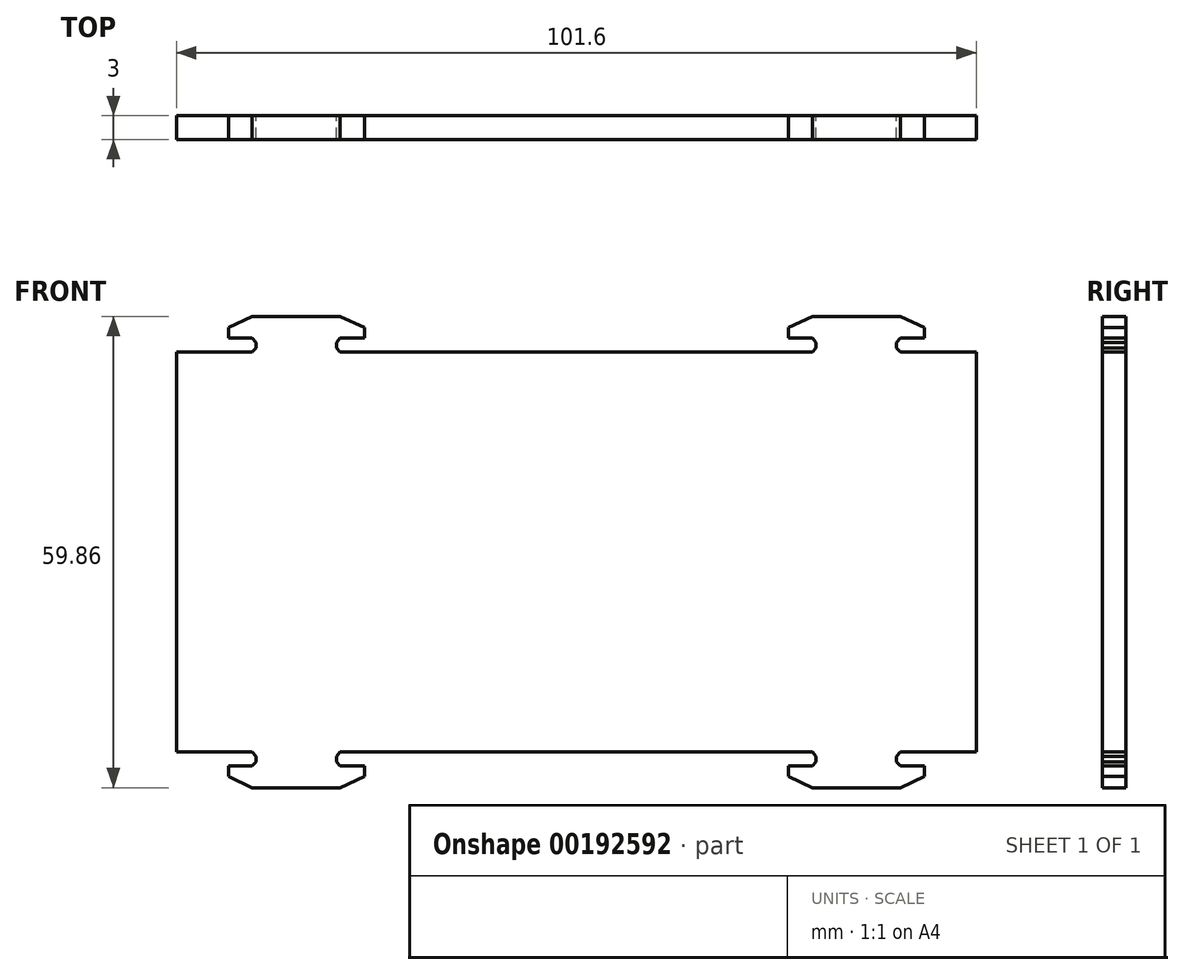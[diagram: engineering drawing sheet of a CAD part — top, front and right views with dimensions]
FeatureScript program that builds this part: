
annotation { "Feature Type Name" : "Feature", "Feature Type Description" : "" }
export const myFeature = defineFeature(function(context is Context, id is Id, definition is map)
    precondition{}
    {
        {
            var Q0;
            Q0=qCreatedBy(makeId("Front.planeOp"),FACE);
            var sketch = newSketch(context, id + "F0", { "sketchPlane" : qUnion([Q0])});
            skLineSegment(sketch, "E0.bottom", {"start": v(50.8, -25.4) * mm, "end": v(-50.8, -25.4) * mm});
            skLineSegment(sketch, "E0.top", {"start": v(50.8, 25.4) * mm, "end": v(-50.8, 25.4) * mm});
            skLineSegment(sketch, "E0.left", {"start": v(50.8, -25.4) * mm, "end": v(50.8, 25.4) * mm});
            skLineSegment(sketch, "E0.right", {"start": v(-50.8, -25.4) * mm, "end": v(-50.8, 25.4) * mm});
            skPoint(sketch, "E0.middle", {"position": v(0, 0) * mm});
            skLineSegment(sketch, "E1", {"start": v(-30.02, 29.93) * mm, "end": v(-41.2, 29.93) * mm});
            skLineSegment(sketch, "E2", {"start": v(-44.2, 28.5) * mm, "end": v(-41.2, 29.93) * mm});
            skLineSegment(sketch, "E3", {"start": v(-26.92, 28.5) * mm, "end": v(-30.02, 29.93) * mm});
            skPoint(sketch, "E4.orphan", {"position": v(-44.2, 29.93) * mm});
            skPoint(sketch, "E5.orphan", {"position": v(-26.92, 29.93) * mm});
            skLineSegment(sketch, "E6", {"start": v(-44.2, 27.17) * mm, "end": v(-41.2, 27.17) * mm});
            skLineSegment(sketch, "E7", {"start": v(-41.2, 27.17) * mm, "end": v(-40.68, 26.65) * mm});
            skLineSegment(sketch, "E8", {"start": v(-40.68, 26.65) * mm, "end": v(-40.68, 25.94) * mm});
            skLineSegment(sketch, "E9", {"start": v(-40.68, 25.94) * mm, "end": v(-41.2, 25.4) * mm});
            skLineSegment(sketch, "E10", {"start": v(-26.92, 27.17) * mm, "end": v(-30.02, 27.17) * mm});
            skLineSegment(sketch, "E11", {"start": v(-30.02, 27.17) * mm, "end": v(-30.47, 26.65) * mm});
            skLineSegment(sketch, "E12", {"start": v(-30.47, 26.65) * mm, "end": v(-30.47, 25.94) * mm});
            skLineSegment(sketch, "E13", {"start": v(-30.47, 25.94) * mm, "end": v(-30.02, 25.4) * mm});
            skLineSegment(sketch, "E14.trimOffspring", {"start": v(-44.2, 27.17) * mm, "end": v(-44.2, 28.5) * mm});
            skLineSegment(sketch, "E15.trimOffspring", {"start": v(-26.92, 27.17) * mm, "end": v(-26.92, 28.5) * mm});
            skLineSegment(sketch, "E16.MirrorCS", {"start": v(30.47, 26.65) * mm, "end": v(30.47, 25.94) * mm});
            skLineSegment(sketch, "E17.MirrorCS", {"start": v(30.02, 27.17) * mm, "end": v(30.47, 26.65) * mm});
            skLineSegment(sketch, "E18.MirrorCS", {"start": v(41.2, 27.17) * mm, "end": v(40.68, 26.65) * mm});
            skLineSegment(sketch, "E19.MirrorCS", {"start": v(40.68, 26.65) * mm, "end": v(40.68, 25.94) * mm});
            skLineSegment(sketch, "E20.MirrorCS", {"start": v(40.68, 25.94) * mm, "end": v(41.2, 25.4) * mm});
            skLineSegment(sketch, "E21.MirrorCS", {"start": v(30.47, 25.94) * mm, "end": v(30.02, 25.4) * mm});
            skLineSegment(sketch, "E22.MirrorCS", {"start": v(26.92, 27.17) * mm, "end": v(26.92, 28.5) * mm});
            skLineSegment(sketch, "E23.MirrorCS", {"start": v(26.92, 27.17) * mm, "end": v(30.02, 27.17) * mm});
            skLineSegment(sketch, "E24.MirrorCS", {"start": v(-50.8, 25.4) * mm, "end": v(50.8, 25.4) * mm});
            skLineSegment(sketch, "E25.MirrorCS", {"start": v(44.2, 27.17) * mm, "end": v(44.2, 28.5) * mm});
            skLineSegment(sketch, "E26.MirrorCS", {"start": v(44.2, 27.17) * mm, "end": v(41.2, 27.17) * mm});
            skPoint(sketch, "E27.MirrorP", {"position": v(44.2, 29.93) * mm});
            skLineSegment(sketch, "E28.MirrorCS", {"start": v(30.02, 29.93) * mm, "end": v(41.2, 29.93) * mm});
            skLineSegment(sketch, "E29.MirrorCS", {"start": v(44.2, 28.5) * mm, "end": v(41.2, 29.93) * mm});
            skPoint(sketch, "E30.MirrorP", {"position": v(26.92, 29.93) * mm});
            skLineSegment(sketch, "E31.MirrorCS", {"start": v(26.92, 28.5) * mm, "end": v(30.02, 29.93) * mm});
            skLineSegment(sketch, "E32.MirrorCS", {"start": v(-41.2, -27.17) * mm, "end": v(-40.68, -26.65) * mm});
            skLineSegment(sketch, "E33.MirrorCS", {"start": v(-30.47, -26.65) * mm, "end": v(-30.47, -25.94) * mm});
            skLineSegment(sketch, "E34.MirrorCS", {"start": v(-40.68, -26.65) * mm, "end": v(-40.68, -25.94) * mm});
            skLineSegment(sketch, "E35.MirrorCS", {"start": v(-40.68, -25.94) * mm, "end": v(-41.2, -25.4) * mm});
            skLineSegment(sketch, "E36.MirrorCS", {"start": v(-30.47, -25.94) * mm, "end": v(-30.02, -25.4) * mm});
            skLineSegment(sketch, "E37.MirrorCS", {"start": v(-44.2, -27.17) * mm, "end": v(-44.2, -28.5) * mm});
            skLineSegment(sketch, "E38.MirrorCS", {"start": v(-30.02, -27.17) * mm, "end": v(-30.47, -26.65) * mm});
            skLineSegment(sketch, "E39.MirrorCS", {"start": v(-26.92, -27.17) * mm, "end": v(-26.92, -28.5) * mm});
            skLineSegment(sketch, "E40.MirrorCS", {"start": v(-26.92, -28.5) * mm, "end": v(-30.02, -29.93) * mm});
            skLineSegment(sketch, "E41.MirrorCS", {"start": v(-44.2, -27.17) * mm, "end": v(-41.2, -27.17) * mm});
            skLineSegment(sketch, "E42.MirrorCS", {"start": v(-26.92, -27.17) * mm, "end": v(-30.02, -27.17) * mm});
            skPoint(sketch, "E43.MirrorP", {"position": v(-26.92, -29.93) * mm});
            skLineSegment(sketch, "E44.MirrorCS", {"start": v(-44.2, -28.5) * mm, "end": v(-41.2, -29.93) * mm});
            skPoint(sketch, "E45.MirrorP", {"position": v(-44.2, -29.93) * mm});
            skLineSegment(sketch, "E46.MirrorCS", {"start": v(-30.02, -29.93) * mm, "end": v(-41.2, -29.93) * mm});
            skLineSegment(sketch, "E47.MirrorCS", {"start": v(30.47, -26.65) * mm, "end": v(30.47, -25.94) * mm});
            skLineSegment(sketch, "E48.MirrorCS", {"start": v(40.68, -25.94) * mm, "end": v(41.2, -25.4) * mm});
            skLineSegment(sketch, "E49.MirrorCS", {"start": v(41.2, -27.17) * mm, "end": v(40.68, -26.65) * mm});
            skLineSegment(sketch, "E50.MirrorCS", {"start": v(30.47, -25.94) * mm, "end": v(30.02, -25.4) * mm});
            skLineSegment(sketch, "E51.MirrorCS", {"start": v(40.68, -26.65) * mm, "end": v(40.68, -25.94) * mm});
            skLineSegment(sketch, "E52.MirrorCS", {"start": v(30.02, -27.17) * mm, "end": v(30.47, -26.65) * mm});
            skLineSegment(sketch, "E53.MirrorCS", {"start": v(26.92, -28.5) * mm, "end": v(30.02, -29.93) * mm});
            skPoint(sketch, "E54.MirrorP", {"position": v(26.92, -29.93) * mm});
            skLineSegment(sketch, "E55.MirrorCS", {"start": v(26.92, -27.17) * mm, "end": v(30.02, -27.17) * mm});
            skLineSegment(sketch, "E56.MirrorCS", {"start": v(30.02, -29.93) * mm, "end": v(41.2, -29.93) * mm});
            skLineSegment(sketch, "E57.MirrorCS", {"start": v(44.2, -27.17) * mm, "end": v(41.2, -27.17) * mm});
            skLineSegment(sketch, "E58.MirrorCS", {"start": v(26.92, -27.17) * mm, "end": v(26.92, -28.5) * mm});
            skLineSegment(sketch, "E59.MirrorCS", {"start": v(44.2, -27.17) * mm, "end": v(44.2, -28.5) * mm});
            skPoint(sketch, "E60.MirrorP", {"position": v(44.2, -29.93) * mm});
            skLineSegment(sketch, "E61.MirrorCS", {"start": v(44.2, -28.5) * mm, "end": v(41.2, -29.93) * mm});
            skSolve(sketch);
        }
        {
            var Q0;
            {var subQ1=sQuery(id+"F0.wireOp",EDGE,"E0.left");Q0=makeQuery(id+"F0.imprint","IMPRINT",FACE,{"disambiguationData":[TD([[makeQuery(id+"F0.imprint","IMPRINT",EDGE,{"derivedFrom":subQ1}),1.0]])]});}
            var Q1;
            Q1=makeQuery(id+"F0.imprint","IMPRINT",FACE,{"disambiguationData":[TD([[makeQuery(id+"F0.imprint","IMPRINT",EDGE,{"derivedFrom":sQuery(id+"F0.wireOp",EDGE,"E1")}),1.0]])]});
            var Q2;
            Q2=makeQuery(id+"F0.imprint","IMPRINT",FACE,{"disambiguationData":[TD([[makeQuery(id+"F0.imprint","IMPRINT",EDGE,{"derivedFrom":sQuery(id+"F0.wireOp",EDGE,"E16.MirrorCS")}),1.0]])]});
            var Q3;
            Q3=makeQuery(id+"F0.imprint","IMPRINT",FACE,{"disambiguationData":[TD([[makeQuery(id+"F0.imprint","IMPRINT",EDGE,{"derivedFrom":sQuery(id+"F0.wireOp",EDGE,"E47.MirrorCS")}),-1.0]])]});
            var Q4;
            Q4=makeQuery(id+"F0.imprint","IMPRINT",FACE,{"disambiguationData":[TD([[makeQuery(id+"F0.imprint","IMPRINT",EDGE,{"derivedFrom":sQuery(id+"F0.wireOp",EDGE,"E32.MirrorCS")}),-1.0]])]});
            extrude(context, id + "F1", {"entities" : qUnion([Q0, Q1, Q2, Q3, Q4]), "depth" : 3 * mm});
        }
    });
